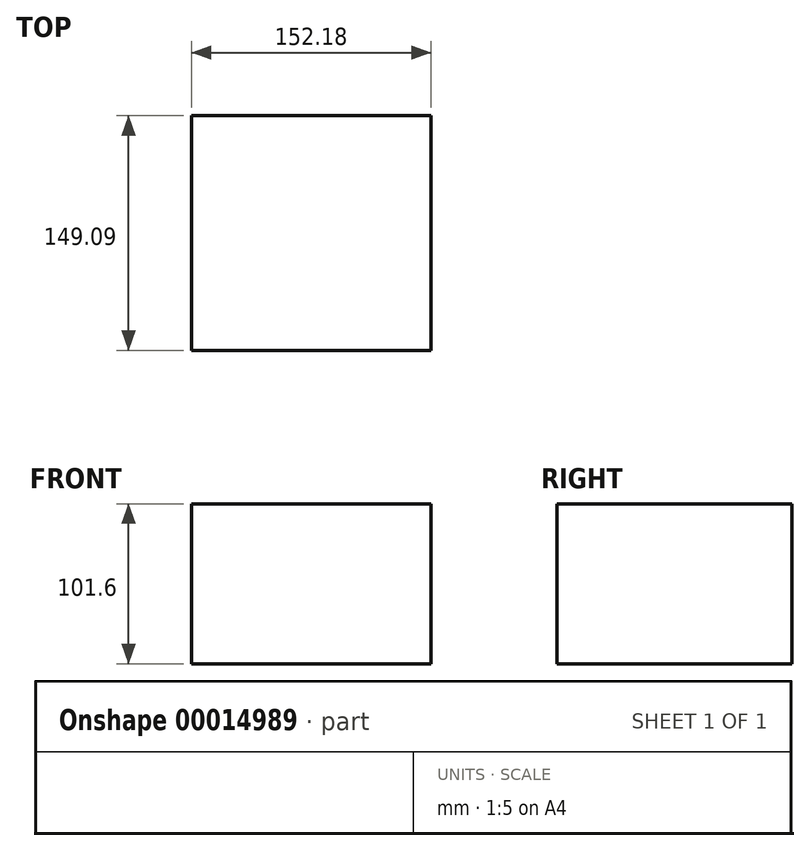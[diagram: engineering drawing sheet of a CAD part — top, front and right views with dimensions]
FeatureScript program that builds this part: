
annotation { "Feature Type Name" : "Feature", "Feature Type Description" : "" }
export const myFeature = defineFeature(function(context is Context, id is Id, definition is map)
    precondition{}
    {
        {
            var Q0;
            Q0=qCreatedBy(makeId("Top.planeOp"),FACE);
            var sketch = newSketch(context, id + "F0", { "sketchPlane" : qUnion([Q0])});
            skLineSegment(sketch, "E0.bottom", {"start": v(-76.06, -75.04) * mm, "end": v(76.12, -75.04) * mm});
            skLineSegment(sketch, "E0.top", {"start": v(-76.06, 74.05) * mm, "end": v(76.12, 74.05) * mm});
            skLineSegment(sketch, "E0.left", {"start": v(-76.06, -75.04) * mm, "end": v(-76.06, 74.05) * mm});
            skLineSegment(sketch, "E0.right", {"start": v(76.12, -75.04) * mm, "end": v(76.12, 74.05) * mm});
            skSolve(sketch);
        }
        {
            var Q0;
            Q0=makeQuery(id+"F0.imprint","IMPRINT",FACE,{"disambiguationData":[TD([[makeQuery(id+"F0.imprint","IMPRINT",EDGE,{"derivedFrom":sQuery(id+"F0.wireOp",EDGE,"E0.bottom")}),1.0]])]});
            extrude(context, id + "F1", {"entities" : qUnion([Q0]), "depth" : 101.6 * mm});
        }
    });
